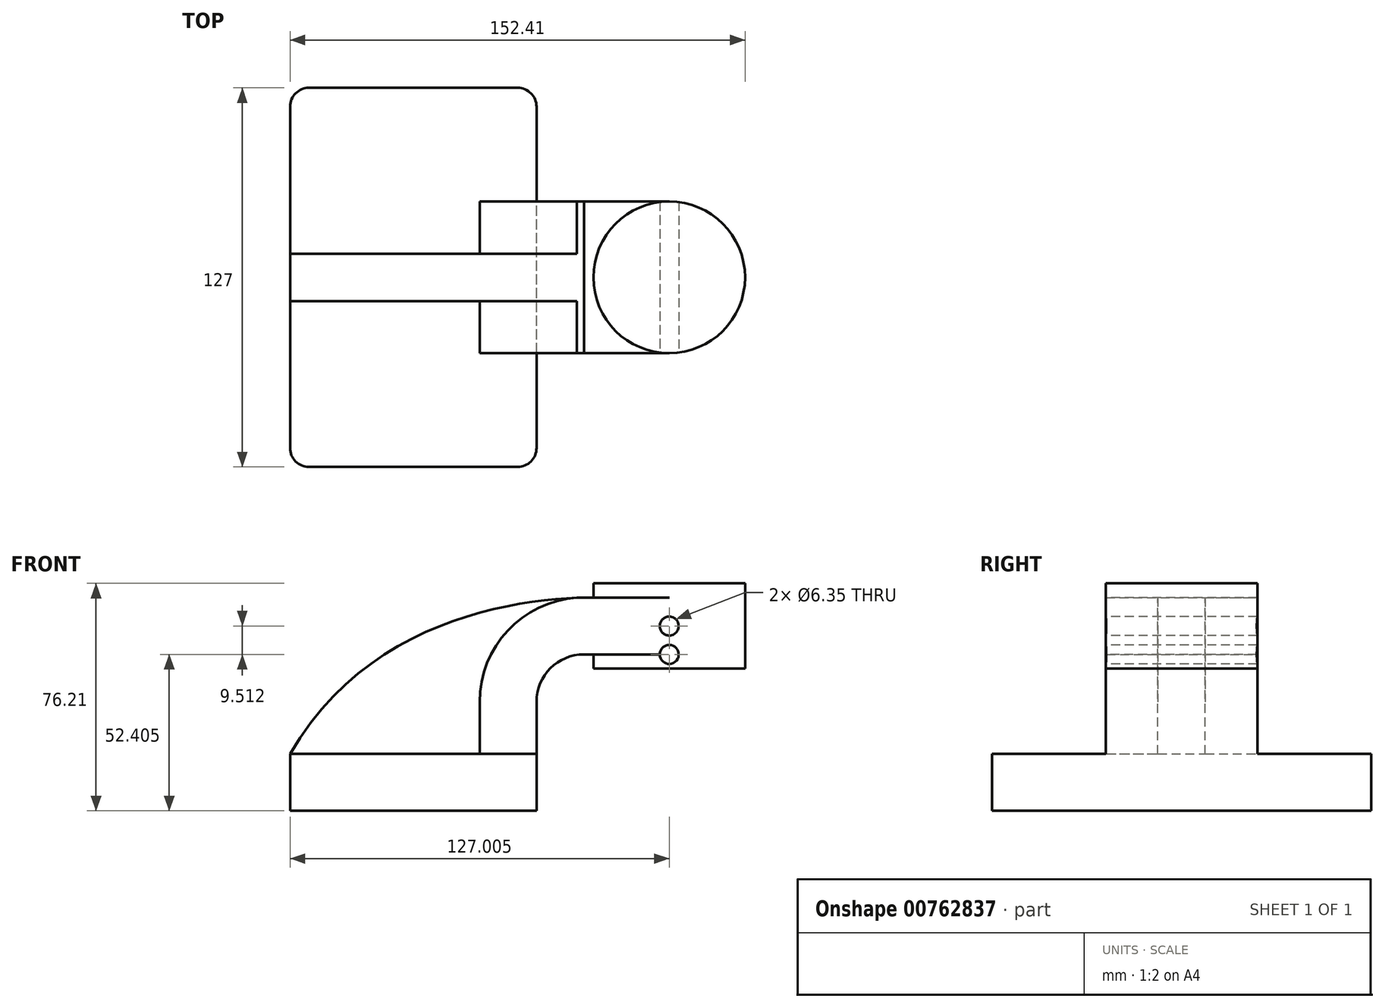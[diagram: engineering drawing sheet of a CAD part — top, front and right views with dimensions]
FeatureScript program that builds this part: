
annotation { "Feature Type Name" : "Feature", "Feature Type Description" : "" }
export const myFeature = defineFeature(function(context is Context, id is Id, definition is map)
    precondition{}
    {
        {
            var Q0;
            Q0=qCreatedBy(makeId("Front.planeOp"),FACE);
            var sketch = newSketch(context, id + "F0", { "sketchPlane" : qUnion([Q0])});
            skLineSegment(sketch, "E0.bottom", {"start": v(41.28, -9.52) * mm, "end": v(-41.28, -9.53) * mm});
            skLineSegment(sketch, "E0.top", {"start": v(41.28, 9.53) * mm, "end": v(-41.28, 9.52) * mm});
            skLineSegment(sketch, "E0.left", {"start": v(41.28, -9.52) * mm, "end": v(41.28, 9.53) * mm});
            skLineSegment(sketch, "E0.right", {"start": v(-41.28, -9.53) * mm, "end": v(-41.28, 9.52) * mm});
            skPoint(sketch, "E0.middle", {"position": v(0, 0) * mm});
            skLineSegment(sketch, "E1.bottom", {"start": v(111.13, 38.1) * mm, "end": v(60.32, 38.1) * mm});
            skLineSegment(sketch, "E1.top", {"start": v(111.13, 66.67) * mm, "end": v(60.32, 66.67) * mm});
            skLineSegment(sketch, "E1.left", {"start": v(111.13, 38.1) * mm, "end": v(111.13, 66.67) * mm});
            skLineSegment(sketch, "E1.right", {"start": v(60.32, 38.1) * mm, "end": v(60.32, 66.67) * mm});
            skPoint(sketch, "E1.middle", {"position": v(85.73, 52.39) * mm});
            skLineSegment(sketch, "E2", {"start": v(41.28, 9.53) * mm, "end": v(41.27, 27) * mm});
            skArc(sketch, "E3", {"start": v(41.27, 27) * mm, "mid": v(45.92, 38.23) * mm, "end": v(57.15, 42.88) * mm});
            skLineSegment(sketch, "E4", {"start": v(57.15, 42.88) * mm, "end": v(85.73, 42.88) * mm});
            skLineSegment(sketch, "E5.0", {"start": v(57.15, 61.93) * mm, "end": v(85.73, 61.93) * mm});
            skArc(sketch, "E5.1", {"start": v(22.23, 27) * mm, "mid": v(32.45, 51.7) * mm, "end": v(57.15, 61.93) * mm});
            skLineSegment(sketch, "E5.2", {"start": v(22.23, 9.53) * mm, "end": v(22.22, 27) * mm});
            skLineSegment(sketch, "E6", {"start": v(85.72, 66.67) * mm, "end": v(85.72, 38.1) * mm});
            skFitSpline(sketch, "E7", {"points": [v(-41.28, 9.52) * mm, v(57.15, 61.93) * mm], "startDerivative": vector(75.91, 132.35) * mm, "endDerivative": vector(75.22, 1.92) * mm});
            skSolve(sketch);
        }
        {
            var Q0;
            Q0=makeQuery(id+"F0.imprint","IMPRINT",FACE,{"disambiguationData":[TD([[makeQuery(id+"F0.imprint","IMPRINT",EDGE,{"derivedFrom":sQuery(id+"F0.wireOp",EDGE,"E0.bottom")}),-1.0]])]});
            extrude(context, id + "F1", {"entities" : qUnion([Q0]), "endBound" : BoundingType.SYMMETRIC, "depth" : 127 * mm, "offsetDistance" : 25.4 * mm});
        }
        {
            var Q0;
            {var subQ1=sQuery(id+"F0.wireOp",EDGE,"E2");Q0=makeQuery(id+"F0.imprint","IMPRINT",FACE,{"disambiguationData":[TD([[makeQuery(id+"F0.imprint","IMPRINT",EDGE,{"derivedFrom":subQ1}),1.0]])]});}
            extrude(context, id + "F2", {"entities" : qUnion([Q0]), "operationType" : NewBodyOperationType.ADD, "endBound" : BoundingType.SYMMETRIC, "depth" : 50.8 * mm, "offsetDistance" : 25.4 * mm});
        }
        {
            var Q0;
            {var subQ3=sQuery(id+"F0.wireOp",EDGE,"E5.2");Q0=makeQuery(id+"F0.imprint","IMPRINT",FACE,{"disambiguationData":[TD([[makeQuery(id+"F0.imprint","IMPRINT",EDGE,{"derivedFrom":subQ3}),1.0]])]});}
            extrude(context, id + "F3", {"entities" : qUnion([Q0]), "operationType" : NewBodyOperationType.ADD, "endBound" : BoundingType.SYMMETRIC, "depth" : 15.88 * mm, "offsetDistance" : 25.4 * mm});
        }
        {
            var Q0;
            {var subQ0=sQuery(id+"F0.wireOp",EDGE,"E4");var subQ1=sQuery(id+"F0.wireOp",EDGE,"E1.right");var subQ2=makeQuery(id+"F0.imprint","INTERSECT",VERTEX,{"derivedFrom":[subQ1,subQ0]});Q0=makeQuery(id+"F0.imprint","IMPRINT",FACE,{"disambiguationData":[TD([[makeQuery(id+"F0.imprint","IMPRINT",EDGE,{"disambiguationData":[TD([[subQ2,-1.0]])],"derivedFrom":subQ1}),-1.0]])]});}
            extrude(context, id + "F4", {"entities" : qUnion([Q0]), "operationType" : NewBodyOperationType.ADD, "endBound" : BoundingType.SYMMETRIC, "depth" : 50.8 * mm, "offsetDistance" : 25.4 * mm});
        }
        {
            var Q0;
            {var subQ0=sQuery(id+"F0.wireOp",EDGE,"E1.left");Q0=makeQuery(id+"F0.imprint","IMPRINT",FACE,{"disambiguationData":[TD([[makeQuery(id+"F0.imprint","IMPRINT",EDGE,{"derivedFrom":subQ0}),1.0]])]});}
            var Q1;
            Q1=sQuery(id+"F0.wireOp",EDGE,"E6");
            revolve(context, id + "F5", {"operationType" : NewBodyOperationType.ADD, "surfaceOperationType" : NewSurfaceOperationType.NEW, "entities" : qUnion([Q0]), "axis" : qUnion([Q1]), "revolveType" : RevolveType.FULL});
        }
        {
            var Q0;
            Q0=makeQuery(id+"F1.opExtrude","CAP_EDGE",EDGE,{"disambiguationData":[OSD([sQuery(id+"F0.wireOp",EDGE,"E0.right")])],"isStart":false});
            var Q1;
            Q1=makeQuery(id+"F1.opExtrude","CAP_EDGE",EDGE,{"disambiguationData":[OSD([sQuery(id+"F0.wireOp",EDGE,"E0.left")])],"isStart":false});
            var Q2;
            Q2=makeQuery(id+"F1.opExtrude","CAP_EDGE",EDGE,{"disambiguationData":[OSD([sQuery(id+"F0.wireOp",EDGE,"E0.left")])],"isStart":true});
            var Q3;
            Q3=makeQuery(id+"F1.opExtrude","CAP_EDGE",EDGE,{"disambiguationData":[OSD([sQuery(id+"F0.wireOp",EDGE,"E0.right")])],"isStart":true});
            fillet(context, id + "F6", {"entities" : qUnion([Q0, Q1, Q2, Q3]), "radius" : 6.35 * mm, "tangentPropagation" : true, "allowEdgeOverflow" : false});
        }
        {
            var Q0;
            Q0=sQuery(id+"F0.wireOp",VERTEX,"E1.middle");
            var Q1;
            Q1=sQuery(id+"F0.wireOp",VERTEX,"E4.end");
            var Q2;
            Q2=makeQuery(id+"F1.opExtrude","SWEPT_BODY",BODY,{"disambiguationData":[OSD([sQuery(id+"F0.wireOp",EDGE,"E0.bottom"),sQuery(id+"F0.wireOp",EDGE,"E0.top"),sQuery(id+"F0.wireOp",EDGE,"E0.left"),sQuery(id+"F0.wireOp",EDGE,"E0.right")])]});
            hole(context, id + "F7", {"style" : HoleStyle.SIMPLE, "endStyle" : HoleEndStyle.THROUGH, "holeDiameter" : 6.35 * mm, "majorDiameter" : 6.35 * mm, "isTappedThrough" : true, "tappedDepth" : 12.7 * mm, "tapClearance" : 3, "locations" : qUnion([Q0, Q1]), "scope" : qUnion([Q2])});
        }
        {
            var Q0;
            Q0=sQuery(id+"F0.wireOp",VERTEX,"E1.middle");
            var Q1;
            Q1=sQuery(id+"F0.wireOp",VERTEX,"E4.end");
            var Q2;
            Q2=makeQuery(id+"F1.opExtrude","SWEPT_BODY",BODY,{"disambiguationData":[OSD([sQuery(id+"F0.wireOp",EDGE,"E0.bottom"),sQuery(id+"F0.wireOp",EDGE,"E0.top"),sQuery(id+"F0.wireOp",EDGE,"E0.left"),sQuery(id+"F0.wireOp",EDGE,"E0.right")])]});
            hole(context, id + "F8", {"style" : HoleStyle.SIMPLE, "endStyle" : HoleEndStyle.THROUGH, "oppositeDirection" : true, "holeDiameter" : 6.35 * mm, "majorDiameter" : 6.35 * mm, "isTappedThrough" : true, "tappedDepth" : 12.7 * mm, "tapClearance" : 3, "locations" : qUnion([Q0, Q1]), "scope" : qUnion([Q2])});
        }
    });
